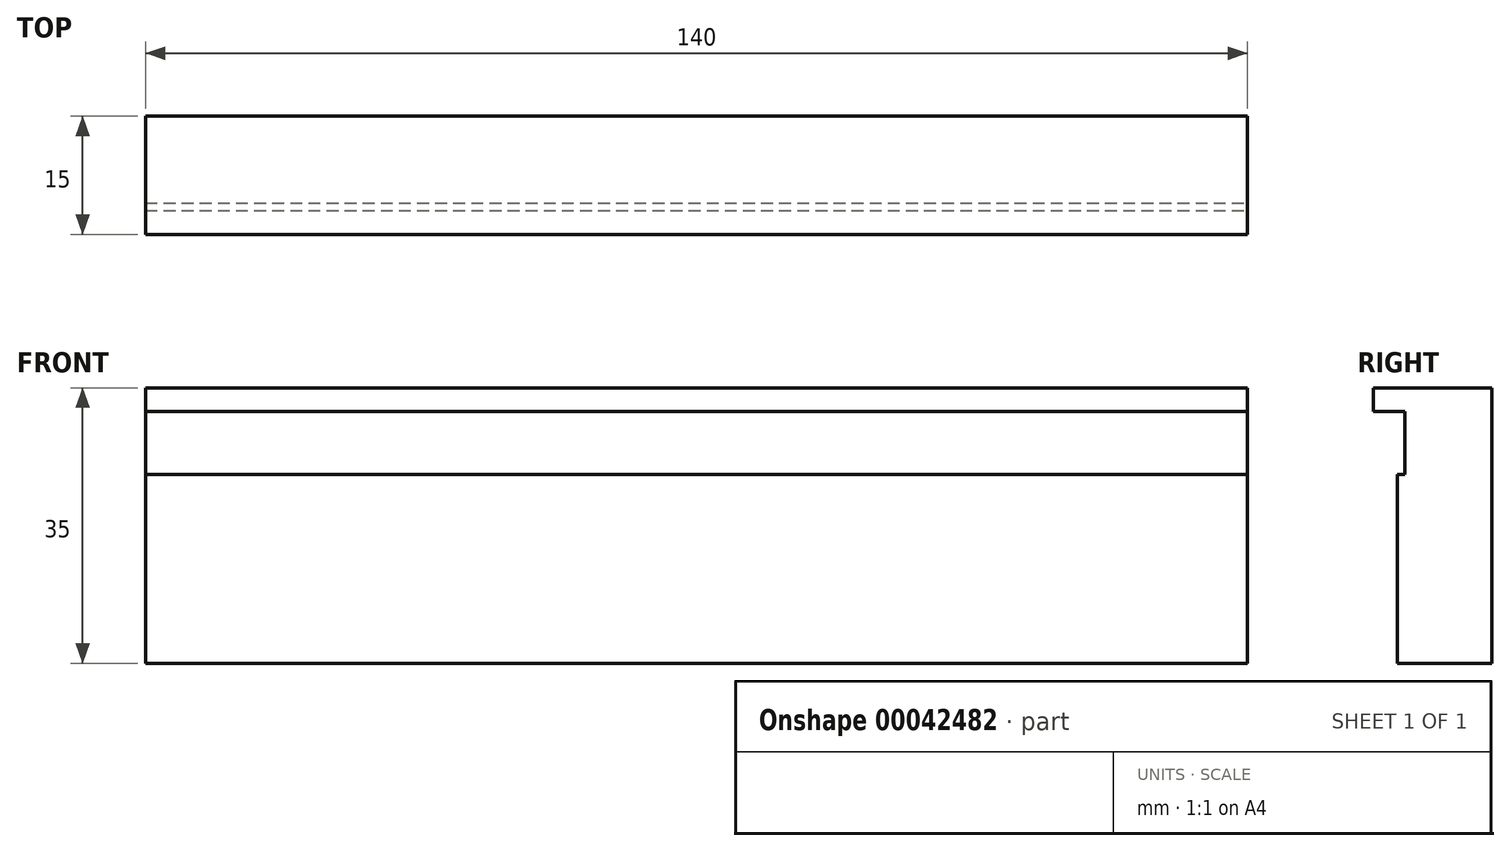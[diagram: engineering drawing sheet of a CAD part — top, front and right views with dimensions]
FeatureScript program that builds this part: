
annotation { "Feature Type Name" : "Feature", "Feature Type Description" : "" }
export const myFeature = defineFeature(function(context is Context, id is Id, definition is map)
    precondition{}
    {
        {
            var Q0;
            Q0=qCreatedBy(makeId("Front.planeOp"),FACE);
            var sketch = newSketch(context, id + "F0", { "sketchPlane" : qUnion([Q0])});
            skLineSegment(sketch, "E0.rect.bottom", {"start": v(-70, 17.5) * mm, "end": v(70, 17.5) * mm});
            skLineSegment(sketch, "E0.rect.top", {"start": v(-70, -17.5) * mm, "end": v(70, -17.5) * mm});
            skLineSegment(sketch, "E0.rect.left", {"start": v(-70, 17.5) * mm, "end": v(-70, -17.5) * mm});
            skLineSegment(sketch, "E0.rect.right", {"start": v(70, 17.5) * mm, "end": v(70, -17.5) * mm});
            skPoint(sketch, "E0.rect.middle", {"position": v(0, 0) * mm});
            skSolve(sketch);
        }
        {
            var Q0;
            Q0=makeQuery(id+"F0.imprint","IMPRINT",FACE,{"disambiguationData":[TD([[makeQuery(id+"F0.imprint","IMPRINT",EDGE,{"derivedFrom":sQuery(id+"F0.wireOp",EDGE,"E0.rect.bottom")}),-1.0]])]});
            extrude(context, id + "F1", {"entities" : qUnion([Q0]), "depth" : 15 * mm});
        }
        {
            var Q0;
            Q0=makeQuery(id+"F1.opExtrude","SWEPT_FACE",FACE,{"disambiguationData":[OSD([sQuery(id+"F0.wireOp",EDGE,"E0.rect.right")])]});
            var sketch = newSketch(context, id + "F2", { "sketchPlane" : qUnion([Q0])});
            skLineSegment(sketch, "E1", {"start": v(-15, -17.5) * mm, "end": v(-15, 14.5) * mm});
            skLineSegment(sketch, "E2", {"start": v(-15, 14.5) * mm, "end": v(-11, 14.5) * mm});
            skLineSegment(sketch, "E3", {"start": v(-11, 14.5) * mm, "end": v(-11, 6.5) * mm});
            skLineSegment(sketch, "E4", {"start": v(-11, 6.5) * mm, "end": v(-12, 6.5) * mm});
            skLineSegment(sketch, "E5", {"start": v(-12, 6.5) * mm, "end": v(-12, -17.5) * mm});
            skLineSegment(sketch, "E6", {"start": v(-12, -17.5) * mm, "end": v(-15, -17.5) * mm});
            skSolve(sketch);
        }
        {
            var Q0;
            Q0=makeQuery(id+"F2.imprint","IMPRINT",FACE,{"disambiguationData":[TD([[makeQuery(id+"F2.imprint","IMPRINT",EDGE,{"derivedFrom":sQuery(id+"F2.wireOp",EDGE,"E1")}),1.0]])]});
            extrude(context, id + "F3", {"entities" : qUnion([Q0]), "operationType" : NewBodyOperationType.REMOVE, "endBound" : BoundingType.UP_TO_NEXT, "oppositeDirection" : true, "depth" : 25 * mm});
        }
    });
